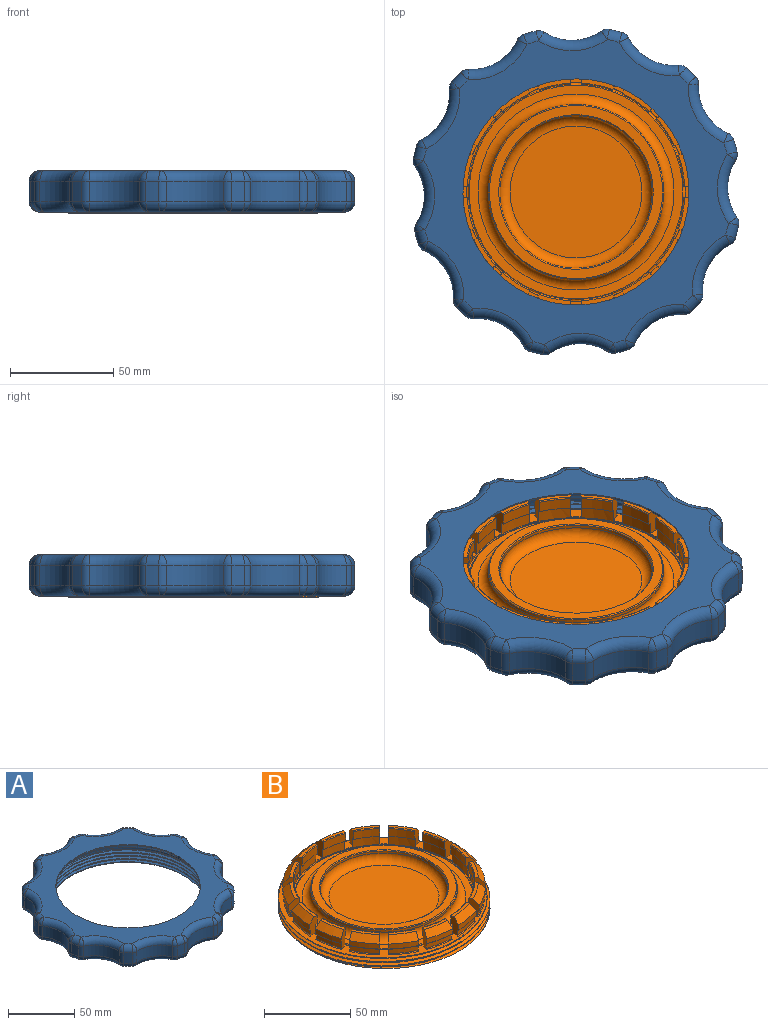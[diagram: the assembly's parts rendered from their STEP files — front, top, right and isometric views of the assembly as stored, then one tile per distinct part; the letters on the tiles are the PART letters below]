
ASSEMBLY  parts=2 mates=1
PART A: 155 faces, bbox 158.6x158.6x23.2 mm
  f0: bspline ~141.61x122.64mm, area 2493mm2, adj f1,f3,f5,f34
  f1: bspline ~142.24x123.18mm, area 1021.4mm2, adj f0,f2,f5,f34
  f2: bspline ~141.61x122.64mm, area 2497.2mm2, adj f1,f3,f5,f34
  f3: cylinder r=59.7mm len=119.39mm, axis (0,0,-1), area 655.8mm2, adj f0,f2,f5,f34
  f4: plane 146.88x146.88mm, normal (0,0,1), area 6544.3mm2, adj f6,f35,f38,f42,f47,f52,f57,f62
  f5: plane 148.6x148.6mm, normal (0,0,-1), area 4416.5mm2, adj f0,f1,f2,f3,f40,f49,f50,f59
  f6: cylinder r=54.7mm len=109.39mm, axis (0,0,1), area 343.7mm2, adj f4,f8
  f7: plane 124.39x124.39mm, normal (0,0,-1), area 957.3mm2, adj f8,f33
  f8: cone r=59.7mm half-angle=45deg, axis (0,0,-1), area 2541.2mm2, adj f6,f7
  f9: cylinder r=80.29mm len=10mm, axis (0,0,1), area 63.4mm2, adj f117,f118,f128,f129
  f10: cylinder r=24.7mm len=27.61mm, axis (0,0,1), area 293mm2, adj f107,f108,f118,f119
  f11: cylinder r=80.29mm len=10mm, axis (0,0,1), area 63.4mm2, adj f97,f98,f108,f109
  f12: cylinder r=24.7mm len=23.91mm, axis (0,0,1), area 293mm2, adj f87,f88,f98,f99
  f13: cylinder r=80.29mm len=10mm, axis (0,0,1), area 63.4mm2, adj f77,f78,f88,f89
  f14: cylinder r=24.7mm len=23.91mm, axis (0,0,1), area 293mm2, adj f67,f68,f78,f79
  f15: cylinder r=80.29mm len=10mm, axis (0,0,1), area 63.4mm2, adj f57,f58,f68,f69
  f16: cylinder r=24.7mm len=27.61mm, axis (0,0,1), area 293mm2, adj f47,f48,f58,f59
  f17: cylinder r=80.29mm len=10mm, axis (0,0,1), area 63.4mm2, adj f38,f39,f48,f49
  f18: cylinder r=24.7mm len=23.91mm, axis (0,0,1), area 293mm2, adj f35,f39,f40,f41
  f19: cylinder r=80.29mm len=10mm, axis (0,0,1), area 63.4mm2, adj f41,f42,f50,f51
  f20: cylinder r=24.7mm len=23.91mm, axis (0,0,1), area 293mm2, adj f51,f52,f60,f61
  f21: cylinder r=80.29mm len=10mm, axis (0,0,1), area 63.4mm2, adj f61,f62,f70,f71
  f22: cylinder r=24.7mm len=27.61mm, axis (0,0,1), area 293mm2, adj f71,f72,f80,f81
  f23: cylinder r=80.29mm len=10mm, axis (0,0,1), area 63.4mm2, adj f81,f82,f90,f91
  f24: cylinder r=24.7mm len=23.91mm, axis (0,0,1), area 293mm2, adj f91,f92,f100,f101
  f25: cylinder r=80.29mm len=10mm, axis (0,0,1), area 63.4mm2, adj f101,f102,f110,f111
  f26: cylinder r=24.7mm len=23.91mm, axis (0,0,1), area 293mm2, adj f111,f112,f120,f121
  f27: cylinder r=80.29mm len=10mm, axis (0,0,1), area 63.4mm2, adj f121,f122,f130,f131
  f28: cylinder r=24.7mm len=27.61mm, axis (0,0,1), area 293mm2, adj f131,f132,f140,f141
  f29: cylinder r=80.29mm len=10mm, axis (0,0,1), area 63.4mm2, adj f141,f142,f150,f151
  f30: cylinder r=24.7mm len=23.91mm, axis (0,0,1), area 293mm2, adj f127,f128,f138,f139
  f31: cylinder r=24.7mm len=23.91mm, axis (0,0,1), area 293mm2, adj f143,f148,f151,f154
  f32: cylinder r=80.29mm len=10mm, axis (0,0,1), area 63.4mm2, adj f137,f138,f148,f149
  f33: cylinder r=62.2mm len=124.39mm, axis (0,0,1), area 1367.8mm2, adj f7,f34
  f34: plane 126.12x126.12mm, normal (0,0,1), area 626.3mm2, adj f0,f1,f2,f3,f33
  f35: torus R=29.7mm, axis (0,0,-1), area 247mm2, adj f4,f18,f36,f37
  f36: sphere r=5mm, area 20.4mm2, adj f35,f38,f39
  f37: sphere r=5mm, area 20.4mm2, adj f35,f41,f42
  f38: torus R=75.29mm, axis (0,0,-1), area 48.7mm2, adj f4,f17,f36,f43
  f39: cylinder r=5mm len=10mm, axis (0,0,-1), area 40.8mm2, adj f17,f18,f36,f44
  f40: torus R=29.7mm, axis (0,0,-1), area 247mm2, adj f5,f18,f44,f45
  f41: cylinder r=5mm len=10mm, axis (0,0,-1), area 40.8mm2, adj f18,f19,f37,f45
  f42: torus R=75.29mm, axis (0,0,-1), area 48.7mm2, adj f4,f19,f37,f46
  f43: sphere r=5mm, area 29.3mm2, adj f38,f47,f48
  f44: sphere r=5mm, area 20.4mm2, adj f39,f40,f49
  f45: sphere r=5mm, area 20.4mm2, adj f40,f41,f50
  f46: sphere r=5mm, area 20.4mm2, adj f42,f51,f52
  f47: torus R=29.7mm, axis (0,0,-1), area 247mm2, adj f4,f16,f43,f53
  f48: cylinder r=5mm len=10mm, axis (0,0,-1), area 40.8mm2, adj f16,f17,f43,f54
  f49: torus R=75.29mm, axis (0,0,-1), area 48.7mm2, adj f5,f17,f44,f54
  f50: torus R=75.29mm, axis (0,0,-1), area 48.7mm2, adj f5,f19,f45,f55
  f51: cylinder r=5mm len=10mm, axis (0,0,-1), area 40.8mm2, adj f19,f20,f46,f55
  f52: torus R=29.7mm, axis (0,0,-1), area 247mm2, adj f4,f20,f46,f56
  f53: sphere r=5mm, area 20.4mm2, adj f47,f57,f58
  f54: sphere r=5mm, area 20.4mm2, adj f48,f49,f59
  f55: sphere r=5mm, area 20.4mm2, adj f50,f51,f60
  f56: sphere r=5mm, area 20.4mm2, adj f52,f61,f62
  f57: torus R=75.29mm, axis (0,0,-1), area 48.7mm2, adj f4,f15,f53,f63
  f58: cylinder r=5mm len=10mm, axis (0,0,-1), area 40.8mm2, adj f15,f16,f53,f64
  f59: torus R=29.7mm, axis (0,0,-1), area 247mm2, adj f5,f16,f54,f64
  f60: torus R=29.7mm, axis (0,0,-1), area 247mm2, adj f5,f20,f55,f65
  f61: cylinder r=5mm len=10mm, axis (0,0,-1), area 40.8mm2, adj f20,f21,f56,f65
  f62: torus R=75.29mm, axis (0,0,-1), area 48.7mm2, adj f4,f21,f56,f66
  f63: sphere r=5mm, area 24.5mm2, adj f57,f67,f68
  f64: sphere r=5mm, area 20.4mm2, adj f58,f59,f69
  f65: sphere r=5mm, area 20.4mm2, adj f60,f61,f70
  f66: sphere r=5mm, area 20.4mm2, adj f62,f71,f72
  f67: torus R=29.7mm, axis (0,0,-1), area 247mm2, adj f4,f14,f63,f73
  f68: cylinder r=5mm len=10mm, axis (0,0,-1), area 40.8mm2, adj f14,f15,f63,f74
  f69: torus R=75.29mm, axis (0,0,-1), area 48.7mm2, adj f5,f15,f64,f74
  f70: torus R=75.29mm, axis (0,0,-1), area 48.7mm2, adj f5,f21,f65,f75
  f71: cylinder r=5mm len=10mm, axis (0,0,-1), area 40.8mm2, adj f21,f22,f66,f75
  f72: torus R=29.7mm, axis (0,0,-1), area 247mm2, adj f4,f22,f66,f76
  f73: sphere r=5mm, area 27.9mm2, adj f67,f77,f78
  f74: sphere r=5mm, area 24.5mm2, adj f68,f69,f79
  f75: sphere r=5mm, area 20.4mm2, adj f70,f71,f80
  f76: sphere r=5mm, area 20.4mm2, adj f72,f81,f82
  f77: torus R=75.29mm, axis (0,0,-1), area 48.7mm2, adj f4,f13,f73,f83
  f78: cylinder r=5mm len=10mm, axis (0,0,-1), area 40.8mm2, adj f13,f14,f73,f84
  f79: torus R=29.7mm, axis (0,0,-1), area 247mm2, adj f5,f14,f74,f84
  f80: torus R=29.7mm, axis (0,0,-1), area 247mm2, adj f5,f22,f75,f85
  f81: cylinder r=5mm len=10mm, axis (0,0,-1), area 40.8mm2, adj f22,f23,f76,f85
  f82: torus R=75.29mm, axis (0,0,-1), area 48.7mm2, adj f4,f23,f76,f86
  f83: sphere r=5mm, area 20.4mm2, adj f77,f87,f88
  f84: sphere r=5mm, area 20.4mm2, adj f78,f79,f89
  f85: sphere r=5mm, area 20.4mm2, adj f80,f81,f90
  f86: sphere r=5mm, area 20.4mm2, adj f82,f91,f92
  f87: torus R=29.7mm, axis (0,0,-1), area 247mm2, adj f4,f12,f83,f93
  f88: cylinder r=5mm len=10mm, axis (0,0,-1), area 40.8mm2, adj f12,f13,f83,f94
  f89: torus R=75.29mm, axis (0,0,-1), area 48.7mm2, adj f5,f13,f84,f94
  f90: torus R=75.29mm, axis (0,0,-1), area 48.7mm2, adj f5,f23,f85,f95
  f91: cylinder r=5mm len=10mm, axis (0,0,-1), area 40.8mm2, adj f23,f24,f86,f95
  f92: torus R=29.7mm, axis (0,0,-1), area 247mm2, adj f4,f24,f86,f96
  f93: sphere r=5mm, area 23.1mm2, adj f87,f97,f98
  f94: sphere r=5mm, area 13.6mm2, adj f88,f89,f99
  f95: sphere r=5mm, area 20.4mm2, adj f90,f91,f100
  f96: sphere r=5mm, area 20.4mm2, adj f92,f101,f102
  f97: torus R=75.29mm, axis (0,0,-1), area 48.7mm2, adj f4,f11,f93,f103
  f98: cylinder r=5mm len=10mm, axis (0,0,-1), area 40.8mm2, adj f11,f12,f93,f104
  f99: torus R=29.7mm, axis (0,0,-1), area 247mm2, adj f5,f12,f94,f104
  f100: torus R=29.7mm, axis (0,0,-1), area 247mm2, adj f5,f24,f95,f105
  f101: cylinder r=5mm len=10mm, axis (0,0,-1), area 40.8mm2, adj f24,f25,f96,f105
  f102: torus R=75.29mm, axis (0,0,-1), area 48.7mm2, adj f4,f25,f96,f106
  f103: sphere r=5mm, area 20.4mm2, adj f97,f107,f108
  f104: sphere r=5mm, area 10.2mm2, adj f98,f99,f109
  f105: sphere r=5mm, area 20.4mm2, adj f100,f101,f110
  f106: sphere r=5mm, area 20.4mm2, adj f102,f111,f112
  f107: torus R=29.7mm, axis (0,0,-1), area 247mm2, adj f4,f10,f103,f113
  f108: cylinder r=5mm len=10mm, axis (0,0,-1), area 40.8mm2, adj f10,f11,f103,f114
  f109: torus R=75.29mm, axis (0,0,-1), area 48.7mm2, adj f5,f11,f104,f114
  f110: torus R=75.29mm, axis (0,0,-1), area 48.7mm2, adj f5,f25,f105,f115
  f111: cylinder r=5mm len=10mm, axis (0,0,-1), area 40.8mm2, adj f25,f26,f106,f115
  f112: torus R=29.7mm, axis (0,0,-1), area 247mm2, adj f4,f26,f106,f116
  f113: sphere r=5mm, area 29.3mm2, adj f107,f117,f118
  f114: sphere r=5mm, area 27.2mm2, adj f108,f109,f119
  f115: sphere r=5mm, area 20.4mm2, adj f110,f111,f120
  f116: sphere r=5mm, area 20.4mm2, adj f112,f121,f122
  f117: torus R=75.29mm, axis (0,0,-1), area 48.7mm2, adj f4,f9,f113,f123
  f118: cylinder r=5mm len=10mm, axis (0,0,-1), area 40.8mm2, adj f9,f10,f113,f124
  f119: torus R=29.7mm, axis (0,0,-1), area 247mm2, adj f5,f10,f114,f124
  f120: torus R=29.7mm, axis (0,0,-1), area 247mm2, adj f5,f26,f115,f125
  f121: cylinder r=5mm len=10mm, axis (0,0,-1), area 40.8mm2, adj f26,f27,f116,f125
  f122: torus R=75.29mm, axis (0,0,-1), area 48.7mm2, adj f4,f27,f116,f126
  f123: sphere r=5mm, area 20.4mm2, adj f117,f127,f128
  f124: sphere r=5mm, area 15mm2, adj f118,f119,f129
  f125: sphere r=5mm, area 20.4mm2, adj f120,f121,f130
  f126: sphere r=5mm, area 20.4mm2, adj f122,f131,f132
  f127: torus R=29.7mm, axis (0,0,-1), area 247mm2, adj f4,f30,f123,f133
  f128: cylinder r=5mm len=10mm, axis (0,0,-1), area 40.8mm2, adj f9,f30,f123,f134
  f129: torus R=75.29mm, axis (0,0,-1), area 48.7mm2, adj f5,f9,f124,f134
  f130: torus R=75.29mm, axis (0,0,-1), area 48.7mm2, adj f5,f27,f125,f135
  f131: cylinder r=5mm len=10mm, axis (0,0,-1), area 40.8mm2, adj f27,f28,f126,f135
  f132: torus R=29.7mm, axis (0,0,-1), area 247mm2, adj f4,f28,f126,f136
  f133: sphere r=5mm, area 20.4mm2, adj f127,f137,f138
  f134: sphere r=5mm, area 20.4mm2, adj f128,f129,f139
  f135: sphere r=5mm, area 20.4mm2, adj f130,f131,f140
  f136: sphere r=5mm, area 20.4mm2, adj f132,f141,f142
  f137: torus R=75.29mm, axis (0,0,-1), area 48.7mm2, adj f4,f32,f133,f144
  f138: cylinder r=5mm len=10mm, axis (0,0,-1), area 40.8mm2, adj f30,f32,f133,f145
  f139: torus R=29.7mm, axis (0,0,-1), area 247mm2, adj f5,f30,f134,f145
  f140: torus R=29.7mm, axis (0,0,-1), area 247mm2, adj f5,f28,f135,f146
  f141: cylinder r=5mm len=10mm, axis (0,0,-1), area 40.8mm2, adj f28,f29,f136,f146
  f142: torus R=75.29mm, axis (0,0,-1), area 48.7mm2, adj f4,f29,f136,f147
  f143: torus R=29.7mm, axis (0,0,-1), area 247mm2, adj f4,f31,f144,f147
  f144: sphere r=5mm, area 20.4mm2, adj f137,f143,f148
  f145: sphere r=5mm, area 19.8mm2, adj f138,f139,f149
  f146: sphere r=5mm, area 29.3mm2, adj f140,f141,f150
  f147: sphere r=5mm, area 20.4mm2, adj f142,f143,f151
  f148: cylinder r=5mm len=10mm, axis (0,0,-1), area 40.8mm2, adj f31,f32,f144,f152
  f149: torus R=75.29mm, axis (0,0,-1), area 48.7mm2, adj f5,f32,f145,f152
  f150: torus R=75.29mm, axis (0,0,-1), area 48.7mm2, adj f5,f29,f146,f153
  f151: cylinder r=5mm len=10mm, axis (0,0,-1), area 40.8mm2, adj f29,f31,f147,f153
  f152: sphere r=5mm, area 20.4mm2, adj f148,f149,f154
  f153: sphere r=5mm, area 20.4mm2, adj f150,f151,f154
  f154: torus R=29.7mm, axis (0,0,-1), area 247mm2, adj f5,f31,f152,f153
PART B: 210 faces, bbox 124.3x143.3x23 mm
  f0: cylinder r=61.32mm len=122.64mm, axis (0,0,-1), area 387.4mm2, adj f1,f2,f139,f140
  f1: bspline ~141.61x122.64mm, area 1901.3mm2, adj f0,f139,f140,f189
  f2: bspline ~122.54x122.45mm, area 1900.3mm2, adj f0,f139,f140,f189
  f3: cylinder r=53.19mm len=106.39mm, axis (0,0,1), area 1692.3mm2, adj f5,f13,f21,f29,f37,f45,f53,f61
  f4: cylinder r=52.19mm len=12.84mm, axis (0,0,1), area 85.2mm2, adj f5,f170,f171,f174
  f5: plane 13.54x9.5mm, normal (0,0,-1), area 15.7mm2, adj f3,f4,f170,f171
  f6: cone r=54.7mm half-angle=45deg, axis (0,0,-1), area 97.6mm2, adj f9,f11,f170,f171
  f7: cylinder r=57.7mm len=14.62mm, axis (0,0,1), area 61.8mm2, adj f8,f10,f170,f171
  f8: plane 14.98x10.23mm, normal (0,0,-1), area 8.9mm2, adj f7,f170,f171,f196
  f9: cylinder r=58.7mm len=14.95mm, axis (0,0,1), area 63.2mm2, adj f6,f170,f171,f196
  f10: torus R=58.2mm, axis (0,0,1), area 13.9mm2, adj f7,f139,f170,f171
  f11: plane 14.42x10.54mm, normal (0,0,1), area 32.2mm2, adj f6,f170,f171,f174
  f12: cylinder r=52.19mm len=12.84mm, axis (0,0,1), area 85.2mm2, adj f13,f168,f169,f175
  f13: plane 13.54x9.5mm, normal (0,0,-1), area 15.7mm2, adj f3,f12,f168,f169
  f14: cone r=54.7mm half-angle=45deg, axis (0,0,-1), area 97.6mm2, adj f17,f19,f168,f169
  f15: cylinder r=57.7mm len=14.62mm, axis (0,0,1), area 61.8mm2, adj f16,f18,f168,f169
  f16: plane 14.98x10.23mm, normal (0,0,-1), area 8.9mm2, adj f15,f168,f169,f195
  f17: cylinder r=58.7mm len=14.95mm, axis (0,0,1), area 63.2mm2, adj f14,f168,f169,f195
  f18: torus R=58.2mm, axis (0,0,1), area 13.9mm2, adj f15,f139,f168,f169
  f19: plane 14.42x10.54mm, normal (0,0,1), area 32.2mm2, adj f14,f168,f169,f175
  f20: cylinder r=52.19mm len=15.14mm, axis (0,0,1), area 85.2mm2, adj f21,f166,f167,f176
  f21: plane 15.52x4.01mm, normal (0,0,-1), area 15.7mm2, adj f3,f20,f166,f167
  f22: cone r=54.7mm half-angle=45deg, axis (0,0,-1), area 97.6mm2, adj f25,f27,f166,f167
  f23: cylinder r=57.7mm len=17.25mm, axis (0,0,1), area 61.8mm2, adj f24,f26,f166,f167
  f24: plane 17.44x3.93mm, normal (0,0,-1), area 8.9mm2, adj f23,f166,f167,f194
  f25: cylinder r=58.7mm len=17.63mm, axis (0,0,1), area 63.2mm2, adj f22,f166,f167,f194
  f26: torus R=58.2mm, axis (0,0,1), area 13.9mm2, adj f23,f139,f166,f167
  f27: plane 16.1x5.06mm, normal (0,0,1), area 32.2mm2, adj f22,f166,f167,f176
  f28: cylinder r=52.19mm len=15.14mm, axis (0,0,1), area 85.2mm2, adj f29,f164,f165,f177
  f29: plane 15.52x4.01mm, normal (0,0,-1), area 15.7mm2, adj f3,f28,f164,f165
  f30: cone r=54.7mm half-angle=45deg, axis (0,0,-1), area 97.6mm2, adj f33,f35,f164,f165
  f31: cylinder r=57.7mm len=17.25mm, axis (0,0,1), area 61.8mm2, adj f32,f34,f164,f165
  f32: plane 17.44x3.93mm, normal (0,0,-1), area 8.9mm2, adj f31,f164,f165,f193
  f33: cylinder r=58.7mm len=17.63mm, axis (0,0,1), area 63.2mm2, adj f30,f164,f165,f193
  f34: torus R=58.2mm, axis (0,0,1), area 13.9mm2, adj f31,f139,f164,f165
  f35: plane 16.1x5.06mm, normal (0,0,1), area 32.2mm2, adj f30,f164,f165,f177
  f36: cylinder r=52.19mm len=12.84mm, axis (0,0,1), area 85.2mm2, adj f37,f162,f163,f178
  f37: plane 13.54x9.5mm, normal (0,0,-1), area 15.7mm2, adj f3,f36,f162,f163
  f38: cone r=54.7mm half-angle=45deg, axis (0,0,-1), area 97.6mm2, adj f41,f43,f162,f163
  f39: cylinder r=57.7mm len=14.62mm, axis (0,0,1), area 61.8mm2, adj f40,f42,f162,f163
  f40: plane 14.98x10.23mm, normal (0,0,-1), area 8.9mm2, adj f39,f162,f163,f192
  f41: cylinder r=58.7mm len=14.95mm, axis (0,0,1), area 63.2mm2, adj f38,f162,f163,f192
  f42: torus R=58.2mm, axis (0,0,1), area 13.9mm2, adj f39,f139,f162,f163
  f43: plane 14.42x10.54mm, normal (0,0,1), area 32.2mm2, adj f38,f162,f163,f178
  f44: cylinder r=52.19mm len=12.84mm, axis (0,0,1), area 85.2mm2, adj f45,f160,f161,f179
  f45: plane 13.54x9.5mm, normal (0,0,-1), area 15.7mm2, adj f3,f44,f160,f161
  f46: cone r=54.7mm half-angle=45deg, axis (0,0,-1), area 97.6mm2, adj f49,f51,f160,f161
  f47: cylinder r=57.7mm len=14.62mm, axis (0,0,1), area 61.8mm2, adj f48,f50,f160,f161
  f48: plane 14.98x10.23mm, normal (0,0,-1), area 8.9mm2, adj f47,f160,f161,f204
  f49: cylinder r=58.7mm len=14.95mm, axis (0,0,1), area 63.2mm2, adj f46,f160,f161,f204
  f50: torus R=58.2mm, axis (0,0,1), area 13.9mm2, adj f47,f139,f160,f161
  f51: plane 14.42x10.54mm, normal (0,0,1), area 32.2mm2, adj f46,f160,f161,f179
  f52: cylinder r=52.19mm len=15.14mm, axis (0,0,1), area 85.2mm2, adj f53,f158,f159,f180
  f53: plane 15.52x4.01mm, normal (0,0,-1), area 15.7mm2, adj f3,f52,f158,f159
  f54: cone r=54.7mm half-angle=45deg, axis (0,0,-1), area 97.6mm2, adj f57,f59,f158,f159
  f55: cylinder r=57.7mm len=17.25mm, axis (0,0,1), area 61.8mm2, adj f56,f58,f158,f159
  f56: plane 17.44x3.93mm, normal (0,0,-1), area 8.9mm2, adj f55,f158,f159,f205
  f57: cylinder r=58.7mm len=17.63mm, axis (0,0,1), area 63.2mm2, adj f54,f158,f159,f205
  f58: torus R=58.2mm, axis (0,0,1), area 13.9mm2, adj f55,f139,f158,f159
  f59: plane 16.1x5.06mm, normal (0,0,1), area 32.2mm2, adj f54,f158,f159,f180
  f60: cylinder r=52.19mm len=15.14mm, axis (0,0,1), area 85.2mm2, adj f61,f156,f157,f181
  f61: plane 15.52x4.01mm, normal (0,0,-1), area 15.7mm2, adj f3,f60,f156,f157
  f62: cone r=54.7mm half-angle=45deg, axis (0,0,-1), area 97.6mm2, adj f65,f67,f156,f157
  f63: cylinder r=57.7mm len=17.25mm, axis (0,0,1), area 61.8mm2, adj f64,f66,f156,f157
  f64: plane 17.44x3.93mm, normal (0,0,-1), area 8.9mm2, adj f63,f156,f157,f206
  f65: cylinder r=58.7mm len=17.63mm, axis (0,0,1), area 63.2mm2, adj f62,f156,f157,f206
  f66: torus R=58.2mm, axis (0,0,1), area 13.9mm2, adj f63,f139,f156,f157
  f67: plane 16.1x5.06mm, normal (0,0,1), area 32.2mm2, adj f62,f156,f157,f181
  f68: cylinder r=52.19mm len=12.84mm, axis (0,0,1), area 85.2mm2, adj f69,f154,f155,f182
  f69: plane 13.54x9.5mm, normal (0,0,-1), area 15.7mm2, adj f3,f68,f154,f155
  f70: cone r=54.7mm half-angle=45deg, axis (0,0,-1), area 97.6mm2, adj f73,f75,f154,f155
  f71: cylinder r=57.7mm len=14.62mm, axis (0,0,1), area 61.8mm2, adj f72,f74,f154,f155
  f72: plane 14.98x10.23mm, normal (0,0,-1), area 8.9mm2, adj f71,f154,f155,f207
  f73: cylinder r=58.7mm len=14.95mm, axis (0,0,1), area 63.2mm2, adj f70,f154,f155,f207
  f74: torus R=58.2mm, axis (0,0,1), area 13.9mm2, adj f71,f139,f154,f155
  f75: plane 14.42x10.54mm, normal (0,0,1), area 32.2mm2, adj f70,f154,f155,f182
  f76: cylinder r=52.19mm len=12.84mm, axis (0,0,1), area 85.2mm2, adj f77,f152,f153,f183
  f77: plane 13.54x9.5mm, normal (0,0,-1), area 15.7mm2, adj f3,f76,f152,f153
  f78: cone r=54.7mm half-angle=45deg, axis (0,0,-1), area 97.6mm2, adj f81,f83,f152,f153
  f79: cylinder r=57.7mm len=14.62mm, axis (0,0,1), area 61.8mm2, adj f80,f82,f152,f153
  f80: plane 14.98x10.23mm, normal (0,0,-1), area 8.9mm2, adj f79,f152,f153,f203
  f81: cylinder r=58.7mm len=14.95mm, axis (0,0,1), area 63.2mm2, adj f78,f152,f153,f203
  f82: torus R=58.2mm, axis (0,0,1), area 13.9mm2, adj f79,f139,f152,f153
  f83: plane 14.42x10.54mm, normal (0,0,1), area 32.2mm2, adj f78,f152,f153,f183
  f84: cylinder r=52.19mm len=15.14mm, axis (0,0,1), area 85.2mm2, adj f85,f150,f151,f184
  f85: plane 15.52x4.01mm, normal (0,0,-1), area 15.7mm2, adj f3,f84,f150,f151
  f86: cone r=54.7mm half-angle=45deg, axis (0,0,-1), area 97.6mm2, adj f89,f91,f150,f151
  f87: cylinder r=57.7mm len=17.25mm, axis (0,0,1), area 61.8mm2, adj f88,f90,f150,f151
  f88: plane 17.44x3.93mm, normal (0,0,-1), area 8.9mm2, adj f87,f150,f151,f202
  f89: cylinder r=58.7mm len=17.63mm, axis (0,0,1), area 63.2mm2, adj f86,f150,f151,f202
  f90: torus R=58.2mm, axis (0,0,1), area 13.9mm2, adj f87,f139,f150,f151
  f91: plane 16.1x5.06mm, normal (0,0,1), area 32.2mm2, adj f86,f150,f151,f184
  f92: cylinder r=52.19mm len=15.14mm, axis (0,0,1), area 85.2mm2, adj f93,f148,f149,f185
  f93: plane 15.52x4.01mm, normal (0,0,-1), area 15.7mm2, adj f3,f92,f148,f149
  f94: cone r=54.7mm half-angle=45deg, axis (0,0,-1), area 97.6mm2, adj f97,f99,f148,f149
  f95: cylinder r=57.7mm len=17.25mm, axis (0,0,1), area 61.8mm2, adj f96,f98,f148,f149
  f96: plane 17.44x3.93mm, normal (0,0,-1), area 8.9mm2, adj f95,f148,f149,f201
  f97: cylinder r=58.7mm len=17.63mm, axis (0,0,1), area 63.2mm2, adj f94,f148,f149,f201
  f98: torus R=58.2mm, axis (0,0,1), area 13.9mm2, adj f95,f139,f148,f149
  f99: plane 16.1x5.06mm, normal (0,0,1), area 32.2mm2, adj f94,f148,f149,f185
  f100: cylinder r=52.19mm len=12.84mm, axis (0,0,1), area 85.2mm2, adj f101,f146,f147,f186
  f101: plane 13.54x9.5mm, normal (0,0,-1), area 15.7mm2, adj f3,f100,f146,f147
  f102: cone r=54.7mm half-angle=45deg, axis (0,0,-1), area 97.6mm2, adj f105,f107,f146,f147
  f103: cylinder r=57.7mm len=14.62mm, axis (0,0,1), area 61.8mm2, adj f104,f106,f146,f147
  f104: plane 14.98x10.23mm, normal (0,0,-1), area 8.9mm2, adj f103,f146,f147,f200
  f105: cylinder r=58.7mm len=14.95mm, axis (0,0,1), area 63.2mm2, adj f102,f146,f147,f200
  f106: torus R=58.2mm, axis (0,0,1), area 13.9mm2, adj f103,f139,f146,f147
  f107: plane 14.42x10.54mm, normal (0,0,1), area 32.2mm2, adj f102,f146,f147,f186
  f108: cylinder r=52.19mm len=12.84mm, axis (0,0,1), area 85.2mm2, adj f109,f144,f145,f187
  f109: plane 13.54x9.5mm, normal (0,0,-1), area 15.7mm2, adj f3,f108,f144,f145
  f110: cone r=54.7mm half-angle=45deg, axis (0,0,-1), area 97.6mm2, adj f113,f115,f144,f145
  f111: cylinder r=57.7mm len=14.62mm, axis (0,0,1), area 61.8mm2, adj f112,f114,f144,f145
  f112: plane 14.98x10.23mm, normal (0,0,-1), area 8.9mm2, adj f111,f144,f145,f199
  f113: cylinder r=58.7mm len=14.95mm, axis (0,0,1), area 63.2mm2, adj f110,f144,f145,f199
  f114: torus R=58.2mm, axis (0,0,1), area 13.9mm2, adj f111,f139,f144,f145
  f115: plane 14.42x10.54mm, normal (0,0,1), area 32.2mm2, adj f110,f144,f145,f187
  f116: cylinder r=52.19mm len=15.14mm, axis (0,0,1), area 85.2mm2, adj f117,f142,f143,f188
  f117: plane 15.52x4.01mm, normal (0,0,-1), area 15.7mm2, adj f3,f116,f142,f143
  f118: cone r=54.7mm half-angle=45deg, axis (0,0,-1), area 97.6mm2, adj f121,f123,f142,f143
  f119: cylinder r=57.7mm len=17.25mm, axis (0,0,1), area 61.8mm2, adj f120,f122,f142,f143
  f120: plane 17.44x3.93mm, normal (0,0,-1), area 8.9mm2, adj f119,f142,f143,f198
  f121: cylinder r=58.7mm len=17.63mm, axis (0,0,1), area 63.2mm2, adj f118,f142,f143,f198
  f122: torus R=58.2mm, axis (0,0,1), area 13.9mm2, adj f119,f139,f142,f143
  f123: plane 16.1x5.06mm, normal (0,0,1), area 32.2mm2, adj f118,f142,f143,f188
  f124: cylinder r=52.19mm len=15.14mm, axis (0,0,1), area 85.2mm2, adj f125,f141,f172,f173
  f125: plane 15.52x4.01mm, normal (0,0,-1), area 15.7mm2, adj f3,f124,f141,f172
  f126: cone r=54.7mm half-angle=45deg, axis (0,0,-1), area 97.6mm2, adj f129,f138,f141,f172
  f127: cylinder r=57.7mm len=17.25mm, axis (0,0,1), area 61.8mm2, adj f128,f130,f141,f172
  f128: plane 17.44x3.93mm, normal (0,0,-1), area 8.9mm2, adj f127,f141,f172,f197
  f129: cylinder r=58.7mm len=17.63mm, axis (0,0,1), area 63.2mm2, adj f126,f141,f172,f197
  f130: torus R=58.2mm, axis (0,0,1), area 13.9mm2, adj f127,f139,f141,f172
  f131: cylinder r=42.39mm len=84.78mm, axis (0,0,1), area 399.5mm2, adj f191,f208
  f132: plane 103.39x103.39mm, normal (0,0,1), area 1339.3mm2, adj f137,f191
  f133: plane 83.78x83.78mm, normal (0,0,1), area 1127.4mm2, adj f208,f209
  f134: cylinder r=36.86mm len=73.73mm, axis (0,0,1), area 347.4mm2, adj f190,f209
  f135: plane 63.73x63.73mm, normal (0,0,1), area 3189.4mm2, adj f190
  f136: torus R=52.69mm, axis (0,0,1), area 520.1mm2, adj f3,f137
  f137: torus R=51.69mm, axis (0,0,1), area 256.7mm2, adj f132,f136
  f138: plane 16.1x5.06mm, normal (0,0,1), area 32.2mm2, adj f126,f141,f172,f173
  f139: plane 122.47x122.39mm, normal (0,0,1), area 1209.7mm2, adj f0,f1,f2,f3,f10,f18,f26,f34
  f140: plane 122.46x122.38mm, normal (0,0,-1), area 11450mm2, adj f0,f1,f2,f189
  f141: plane 12.01x6.52mm, normal (0,-1,0), area 60mm2, adj f3,f124,f125,f126,f127,f128,f129,f130
  f142: plane 12.01x6.52mm, normal (0,1,0), area 60mm2, adj f3,f116,f117,f118,f119,f120,f121,f122
  f143: plane 12.01x6.02mm, normal (0.38,-0.92,0), area 60mm2, adj f3,f116,f117,f118,f119,f120,f121,f122
  f144: plane 12.01x6.02mm, normal (-0.38,0.92,0), area 60mm2, adj f3,f108,f109,f110,f111,f112,f113,f114
  f145: plane 12.01x4.61mm, normal (0.71,-0.71,0), area 60mm2, adj f3,f108,f109,f110,f111,f112,f113,f114
  f146: plane 12.01x4.61mm, normal (-0.71,0.71,0), area 60mm2, adj f3,f100,f101,f102,f103,f104,f105,f106
  f147: plane 12.01x6.02mm, normal (0.92,-0.38,0), area 60mm2, adj f3,f100,f101,f102,f103,f104,f105,f106
  f148: plane 12.01x6.02mm, normal (-0.92,0.38,0), area 60mm2, adj f3,f92,f93,f94,f95,f96,f97,f98
  f149: plane 12.01x6.52mm, normal (1,0,0), area 60mm2, adj f3,f92,f93,f94,f95,f96,f97,f98
  f150: plane 12.01x6.52mm, normal (-1,0,0), area 60mm2, adj f3,f84,f85,f86,f87,f88,f89,f90
  f151: plane 12.01x6.02mm, normal (0.92,0.38,0), area 60mm2, adj f3,f84,f85,f86,f87,f88,f89,f90
  f152: plane 12.01x6.02mm, normal (-0.92,-0.38,0), area 60mm2, adj f3,f76,f77,f78,f79,f80,f81,f82
  f153: plane 12.01x4.61mm, normal (0.71,0.71,0), area 60mm2, adj f3,f76,f77,f78,f79,f80,f81,f82
  f154: plane 12.01x4.61mm, normal (-0.71,-0.71,0), area 60mm2, adj f3,f68,f69,f70,f71,f72,f73,f74
  f155: plane 12.01x6.02mm, normal (0.38,0.92,0), area 60mm2, adj f3,f68,f69,f70,f71,f72,f73,f74
  f156: plane 12.01x6.02mm, normal (-0.38,-0.92,0), area 60mm2, adj f3,f60,f61,f62,f63,f64,f65,f66
  f157: plane 12.01x6.52mm, normal (0,1,0), area 60mm2, adj f3,f60,f61,f62,f63,f64,f65,f66
  f158: plane 12.01x6.52mm, normal (0,-1,0), area 60mm2, adj f3,f52,f53,f54,f55,f56,f57,f58
  f159: plane 12.01x6.02mm, normal (-0.38,0.92,0), area 60mm2, adj f3,f52,f53,f54,f55,f56,f57,f58
  f160: plane 12.01x6.02mm, normal (0.38,-0.92,0), area 60mm2, adj f3,f44,f45,f46,f47,f48,f49,f50
  f161: plane 12.01x4.61mm, normal (-0.71,0.71,0), area 60mm2, adj f3,f44,f45,f46,f47,f48,f49,f50
  f162: plane 12.01x4.61mm, normal (0.71,-0.71,0), area 60mm2, adj f3,f36,f37,f38,f39,f40,f41,f42
  f163: plane 12.01x6.02mm, normal (-0.92,0.38,0), area 60mm2, adj f3,f36,f37,f38,f39,f40,f41,f42
  f164: plane 12.01x6.02mm, normal (0.92,-0.38,0), area 60mm2, adj f3,f28,f29,f30,f31,f32,f33,f34
  f165: plane 12.01x6.52mm, normal (-1,0,0), area 60mm2, adj f3,f28,f29,f30,f31,f32,f33,f34
  f166: plane 12.01x6.52mm, normal (1,0,0), area 60mm2, adj f3,f20,f21,f22,f23,f24,f25,f26
  f167: plane 12.01x6.02mm, normal (-0.92,-0.38,0), area 60mm2, adj f3,f20,f21,f22,f23,f24,f25,f26
  f168: plane 12.01x6.02mm, normal (0.92,0.38,0), area 60mm2, adj f3,f12,f13,f14,f15,f16,f17,f18
  f169: plane 12.01x4.61mm, normal (-0.71,-0.71,0), area 60mm2, adj f3,f12,f13,f14,f15,f16,f17,f18
  f170: plane 12.01x4.61mm, normal (0.71,0.71,0), area 60mm2, adj f3,f4,f5,f6,f7,f8,f9,f10
  f171: plane 12.01x6.02mm, normal (-0.38,-0.92,0), area 60mm2, adj f3,f4,f5,f6,f7,f8,f9,f10
  f172: plane 12.01x6.02mm, normal (0.38,0.92,0), area 60mm2, adj f3,f124,f125,f126,f127,f128,f129,f130
  f173: torus R=52.69mm, axis (0,0,1), area 12.2mm2, adj f124,f138,f141,f172
  f174: torus R=52.69mm, axis (0,0,1), area 12.2mm2, adj f4,f11,f170,f171
  f175: torus R=52.69mm, axis (0,0,1), area 12.2mm2, adj f12,f19,f168,f169
  f176: torus R=52.69mm, axis (0,0,1), area 12.2mm2, adj f20,f27,f166,f167
  f177: torus R=52.69mm, axis (0,0,1), area 12.2mm2, adj f28,f35,f164,f165
  f178: torus R=52.69mm, axis (0,0,1), area 12.2mm2, adj f36,f43,f162,f163
  f179: torus R=52.69mm, axis (0,0,1), area 12.2mm2, adj f44,f51,f160,f161
  f180: torus R=52.69mm, axis (0,0,1), area 12.2mm2, adj f52,f59,f158,f159
  f181: torus R=52.69mm, axis (0,0,1), area 12.2mm2, adj f60,f67,f156,f157
  f182: torus R=52.69mm, axis (0,0,1), area 12.2mm2, adj f68,f75,f154,f155
  f183: torus R=52.69mm, axis (0,0,1), area 12.2mm2, adj f76,f83,f152,f153
  f184: torus R=52.69mm, axis (0,0,1), area 12.2mm2, adj f84,f91,f150,f151
  f185: torus R=52.69mm, axis (0,0,1), area 12.2mm2, adj f92,f99,f148,f149
  f186: torus R=52.69mm, axis (0,0,1), area 12.2mm2, adj f100,f107,f146,f147
  f187: torus R=52.69mm, axis (0,0,1), area 12.2mm2, adj f108,f115,f144,f145
  f188: torus R=52.69mm, axis (0,0,1), area 12.2mm2, adj f116,f123,f142,f143
  f189: bspline ~137.86x119.39mm, area 905.2mm2, adj f1,f2,f139,f140
  f190: torus R=31.86mm, axis (0,0,1), area 1729.4mm2, adj f134,f135
  f191: torus R=47.39mm, axis (0,0,1), area 2181.6mm2, adj f131,f132
  f192: cone r=58.7mm half-angle=45deg, axis (0,0,1), area 12.7mm2, adj f40,f41,f162,f163
  f193: cone r=58.7mm half-angle=45deg, axis (0,0,1), area 12.7mm2, adj f32,f33,f164,f165
  f194: cone r=58.7mm half-angle=45deg, axis (0,0,1), area 12.7mm2, adj f24,f25,f166,f167
  f195: cone r=58.7mm half-angle=45deg, axis (0,0,1), area 12.7mm2, adj f16,f17,f168,f169
  f196: cone r=58.7mm half-angle=45deg, axis (0,0,1), area 12.7mm2, adj f8,f9,f170,f171
  f197: cone r=58.7mm half-angle=45deg, axis (0,0,1), area 12.7mm2, adj f128,f129,f141,f172
  f198: cone r=58.7mm half-angle=45deg, axis (0,0,1), area 12.7mm2, adj f120,f121,f142,f143
  f199: cone r=58.7mm half-angle=45deg, axis (0,0,1), area 12.7mm2, adj f112,f113,f144,f145
  f200: cone r=58.7mm half-angle=45deg, axis (0,0,1), area 12.7mm2, adj f104,f105,f146,f147
  f201: cone r=58.7mm half-angle=45deg, axis (0,0,1), area 12.7mm2, adj f96,f97,f148,f149
  f202: cone r=58.7mm half-angle=45deg, axis (0,0,1), area 12.7mm2, adj f88,f89,f150,f151
  f203: cone r=58.7mm half-angle=45deg, axis (0,0,1), area 12.7mm2, adj f80,f81,f152,f153
  f204: cone r=58.7mm half-angle=45deg, axis (0,0,1), area 12.7mm2, adj f48,f49,f160,f161
  f205: cone r=58.7mm half-angle=45deg, axis (0,0,1), area 12.7mm2, adj f56,f57,f158,f159
  f206: cone r=58.7mm half-angle=45deg, axis (0,0,1), area 12.7mm2, adj f64,f65,f156,f157
  f207: cone r=58.7mm half-angle=45deg, axis (0,0,1), area 12.7mm2, adj f72,f73,f154,f155
  f208: cone r=41.89mm half-angle=45deg, axis (0,0,-1), area 187.2mm2, adj f131,f133
  f209: cone r=36.86mm half-angle=45deg, axis (0,0,1), area 164.9mm2, adj f133,f134
PLACE A rot(axis=(0,0,-1),178.8deg) t=(-9.53,14.92,-38.77)mm
PLACE B t=(-9.53,14.92,7.21)mm fixed
MATE cylindrical A.f6 <-> B.f134  axis (0,0,1) through (-9.53,14.92,27.78)mm
